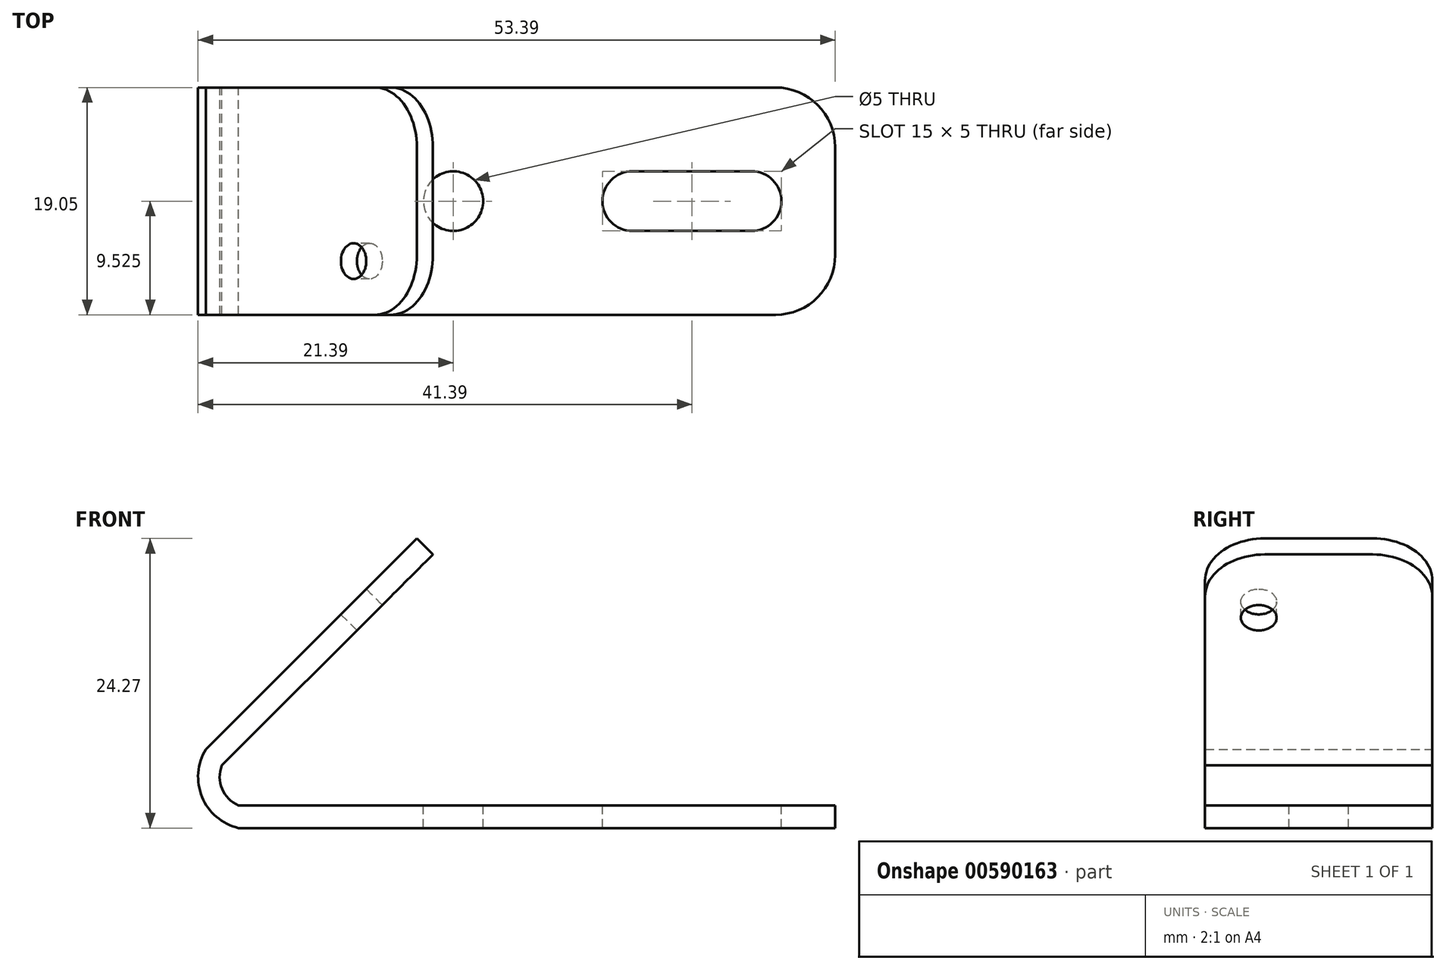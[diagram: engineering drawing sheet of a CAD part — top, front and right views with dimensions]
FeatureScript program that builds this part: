
annotation { "Feature Type Name" : "Feature", "Feature Type Description" : "" }
export const myFeature = defineFeature(function(context is Context, id is Id, definition is map)
    precondition{}
    {
        {
            var Q0;
            Q0=qCreatedBy(makeId("Front.planeOp"),FACE);
            var sketch = newSketch(context, id + "F0", { "sketchPlane" : qUnion([Q0])});
            skLineSegment(sketch, "E0", {"start": v(0, 0) * mm, "end": v(50, 0) * mm});
            skLineSegment(sketch, "E1", {"start": v(50, 0) * mm, "end": v(50, 1.9) * mm});
            skLineSegment(sketch, "E2", {"start": v(50, 1.9) * mm, "end": v(0, 1.9) * mm});
            skLineSegment(sketch, "E3", {"start": v(-2.73, 6.6) * mm, "end": v(14.95, 24.27) * mm});
            skArc(sketch, "E4", {"start": v(-2.73, 6.6) * mm, "mid": v(-3.05, 2.6) * mm, "end": v(0, 0) * mm});
            skLineSegment(sketch, "E5", {"start": v(14.95, 24.27) * mm, "end": v(16.29, 22.93) * mm});
            skLineSegment(sketch, "E6", {"start": v(16.29, 22.93) * mm, "end": v(-1.39, 5.25) * mm});
            skArc(sketch, "E7", {"start": v(0, 1.9) * mm, "mid": v(-1.38, 3.3) * mm, "end": v(-1.39, 5.25) * mm});
            skSolve(sketch);
        }
        {
            var Q0;
            Q0=qSketchRegion(id+"F0",true);
            extrude(context, id + "F1", {"entities" : qUnion([Q0]), "depth" : 19.05 * mm, "offsetDistance" : 25 * mm});
        }
        {
            var Q0;
            Q0=makeQuery(id+"F1.opExtrude","CAP_EDGE",EDGE,{"disambiguationData":[OSD([sQuery(id+"F0.wireOp",EDGE,"E5")])],"isStart":false});
            var Q1;
            Q1=makeQuery(id+"F1.opExtrude","CAP_EDGE",EDGE,{"disambiguationData":[OSD([sQuery(id+"F0.wireOp",EDGE,"E5")])],"isStart":true});
            fillet(context, id + "F2", {"entities" : qUnion([Q0, Q1]), "radius" : 5 * mm, "tangentPropagation" : true, "allowEdgeOverflow" : false});
        }
        {
            var Q0;
            Q0=makeQuery(id+"F1.opExtrude","SWEPT_FACE",FACE,{"disambiguationData":[OSD([sQuery(id+"F0.wireOp",EDGE,"E3")])]});
            var sketch = newSketch(context, id + "F3", { "sketchPlane" : qUnion([Q0])});
            skLineSegment(sketch, "E8", {"start": v(19.05, 27.73) * mm, "end": v(14.55, 27.73) * mm, "construction": true});
            skLineSegment(sketch, "E9", {"start": v(14.55, 27.73) * mm, "end": v(14.55, 20.23) * mm, "construction": true});
            skCircle(sketch, "E10", {"center": v(14.55, 20.23) * mm, "radius": 1.5 * mm});
            skLineSegment(sketch, "E11", {"start": v(9.53, 42.7) * mm, "end": v(9.53, -11.02) * mm, "construction": true});
            skPoint(sketch, "E11.startSnap0", {"position": v(9.53, 27.73) * mm});
            skCircle(sketch, "E12.MirrorC", {"center": v(4.5, 20.23) * mm, "radius": 1.5 * mm});
            skSolve(sketch);
        }
        {
            var Q0;
            Q0=makeQuery(id+"F3.imprint","IMPRINT",FACE,{"disambiguationData":[TD([[makeQuery(id+"F3.imprint","IMPRINT",EDGE,{"derivedFrom":sQuery(id+"F3.wireOp",EDGE,"E10")}),1.0]])]});
            extrude(context, id + "F4", {"entities" : qUnion([Q0]), "operationType" : NewBodyOperationType.REMOVE, "oppositeDirection" : true, "depth" : 10 * mm, "offsetDistance" : 25 * mm});
        }
        {
            var Q0;
            Q0=makeQuery(id+"F1.opExtrude","CAP_EDGE",EDGE,{"disambiguationData":[OSD([sQuery(id+"F0.wireOp",EDGE,"E3")])],"isStart":true});
            cPoint(context, id + "F5", {"entities" : qUnion([Q0]), "parameter" : 0.5});
        }
        {
            var Q0;
            Q0=makeQuery(id+"F1.opExtrude","CAP_EDGE",EDGE,{"disambiguationData":[OSD([sQuery(id+"F0.wireOp",EDGE,"E3")])],"isStart":false});
            cPoint(context, id + "F6", {"entities" : qUnion([Q0]), "parameter" : 0.5});
        }
        {
            var Q0;
            Q0=qCreatedBy(id+"F5",VERTEX);
            var Q1;
            Q1=qCreatedBy(id+"F6",VERTEX);
            cPlane(context, id + "F7", {"entities" : qUnion([Q0, Q1]), "cplaneType" : CPlaneType.MID_PLANE, "offset" : 25 * mm, "width" : 150 * mm, "height" : 150 * mm});
        }
        {
            var Q0;
            Q0=makeQuery(id+"F1.opExtrude","CAP_EDGE",EDGE,{"disambiguationData":[OSD([sQuery(id+"F0.wireOp",EDGE,"E1")])],"isStart":true});
            var Q1;
            Q1=makeQuery(id+"F1.opExtrude","CAP_EDGE",EDGE,{"disambiguationData":[OSD([sQuery(id+"F0.wireOp",EDGE,"E1")])],"isStart":false});
            fillet(context, id + "F8", {"entities" : qUnion([Q0, Q1]), "radius" : 5 * mm, "tangentPropagation" : true, "allowEdgeOverflow" : false});
        }
        {
            var Q0;
            Q0=makeQuery(id+"F1.opExtrude","SWEPT_FACE",FACE,{"disambiguationData":[OSD([sQuery(id+"F0.wireOp",EDGE,"E2")])]});
            var sketch = newSketch(context, id + "F9", { "sketchPlane" : qUnion([Q0])});
            skArc(sketch, "E13", {"start": v(43, -12.03) * mm, "mid": v(45.5, -9.53) * mm, "end": v(43, -7.03) * mm});
            skPoint(sketch, "E13.centerSnap0", {"position": v(50, -9.53) * mm});
            skArc(sketch, "E14", {"start": v(33, -7.03) * mm, "mid": v(30.5, -9.53) * mm, "end": v(33, -12.03) * mm});
            skLineSegment(sketch, "E15", {"start": v(33, -7.03) * mm, "end": v(43, -7.03) * mm});
            skLineSegment(sketch, "E16", {"start": v(33, -12.03) * mm, "end": v(43, -12.03) * mm});
            skCircle(sketch, "E17", {"center": v(18, -9.53) * mm, "radius": 2.5 * mm});
            skSolve(sketch);
        }
        {
            var Q0;
            Q0=makeQuery(id+"F9.imprint","IMPRINT",FACE,{"disambiguationData":[TD([[makeQuery(id+"F9.imprint","IMPRINT",EDGE,{"derivedFrom":sQuery(id+"F9.wireOp",EDGE,"E17")}),1.0]])]});
            var Q1;
            Q1=makeQuery(id+"F9.imprint","IMPRINT",FACE,{"disambiguationData":[TD([[makeQuery(id+"F9.imprint","IMPRINT",EDGE,{"derivedFrom":sQuery(id+"F9.wireOp",EDGE,"E13")}),1.0]])]});
            extrude(context, id + "F10", {"entities" : qUnion([Q0, Q1]), "operationType" : NewBodyOperationType.REMOVE, "oppositeDirection" : true, "depth" : 25 * mm, "offsetDistance" : 25 * mm});
        }
    });
